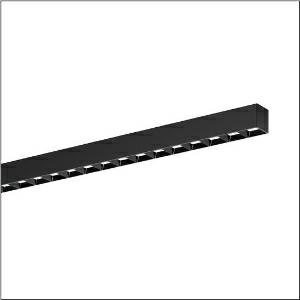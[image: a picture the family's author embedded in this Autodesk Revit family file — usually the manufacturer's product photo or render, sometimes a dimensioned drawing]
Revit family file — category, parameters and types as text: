
# Revit family: silica_r__21_51mx24tctab_feaf
name_source: partatom
category: Lighting Fixtures
units: mm (PartAtom-declared; Revit-internal decimal feet)

## family parameters
Cut with Voids When Loaded = No
Host = Face
Light Source = No
Part Type = Normal
Room Calculation Point = No
Round Connector Dimension = Use Diameter
Shared = No

## types (1)
- --- (1 x LED, 8200 lm, 81.1 W, 6500K)
    Apparent Load = 81 VA
    CIE Flux Codes = 74 94 99 100 100
    Color Rendering = 80
    Color Temperature = 6500K
    Default Elevation = 1800 mm
    Description = Silica® 21, office luminaire, primary light control with darklight reflector, of PMMA, black, light emission: direct distribution, primary light characteristic: asymmetric, installation type: surface-mounted, LED, rated luminous flux: 8.200lm, luminous efficacy: 96lm/W, light colour: 8tw, colour temperature: 2700..6500K, control gear: DALI DT8, with terminal, 3+2-pole, max. 2.5mm², mains connection: 220..240V, AC, 50/60Hz, rated input power: 85.2W, luminaire housing, of aluminium, matt jet black (RAL 9005), length: 3.004mm, width: 53mm, height: 53mm, protection rating (complete): IP20, insulation class (complete): insulation class I (protective earthing), certification: CE, permissible operating ambient temperature: 0..+35°C, standard: EN 50419, packaging unit: 1 piece
    Height = 53 mm
    Lamp = 1 x LED
    Lamp Light Flux = 8200 lm
    Lamp Power = 81.1 W
    Lamp count = 1
    Length = 3004 mm
    Luminous efficacy = 101 lm/W
    Manufacturer = Siteco
    ModVariant = No
    Model = 51MX24TCTAB
    Mounting Place = Ceiling
    Mounting Type = Surface mounted
    Number of Poles = 1
    OnlyDefault = Yes
    Power Factor = 1
    Product Name = Silica® 21
    Product group = office luminaire | ceiling mounted
    ProductGroupID = 302
    Protection Class = Protection class I
    Protection Degree = IP 20
    RLX_Detail_Level = 1
    RLX_Emergency_Light_Flux = 0 lm
    RLX_Emergency_Type = 0
    RLX_Emergency_Type_DB = No
    RlxData = <blob elided: 60905 chars, md5=43a55187>
    Socket = socket
    Standby Power = 0 W
    System Light Flux = 8200 lm
    System Power = 81 W
    Type Comments = individual setting
    Type Image = l_1335908.jpg
    URL = http://relux.com
    VarID = @adj_139986
    Voltage = 0 V
    Weight = 0.00 kg
    Width = 53 mm

## geometry (parser evidence)
native form markers: Blend x4, Sweep x13
no freeform markers — native parametric forms only
